# Revit family: Hager-Univers-IP55-D275-H2050-Cl.I-Steel_encl-NoHosted-PL-en
name_source: partatom
category: Equipement électrique
units: mm (PartAtom-declared; Revit-internal decimal feet)

## family parameters
Basée sur le plan de construction = Oui
Configuration du panneau = Deux colonnes, circuits au sein
Cote de connecteur circulaire = Utiliser le diamètre
Couper avec des vides une fois chargée = Non
Partagée = Non
Point de calcul de pièce = Non
Toujours verticalement = Oui
Type d'élément = Tableau de raccordement

## types (11) — shared parameters
Commentaires du type = Univers
EF000003 - Mounting method = EV012274 - Floor installation
EF000007 - Colour = EV000270 - Grey
EF000040 - Height = 2050 mm  [stored 6.72572 ft]
EF000049 - Depth = 275 mm
EF000116 - RAL-number = 7035
EF000118 - With mounting plate = Non
EF000266 - Number of rows = 12
EF000339 - Type of cover = EV004216 - Door
EF001088 - Extension possible = Oui
EF001131 - Internal depth = 275 mm
EF001596 - Material housing = EV000179 - Steel
EF001613 - Circuit integrity = EV000494 - None
EF002950 - Width in number of modular spacings = 24
EF003532 - Suitable for outdoor use = Non
EF004293 - Impact strength = EV008784 - IK10
EF005474 - Degree of protection (IP) = EV006420 - IP55
EF006306 - With lock = Non
EF007800 - Suitable for lightning protection = Non
EF008873 - Nominal current (In) = 800 A
EF009170 - Material plate thickness cabinet = 2 mm  [stored 0.00656168 ft]
EF009171 - Material plate thickness door/cover = 2 mm  [stored 0.00656168 ft]
EF009212 - Cover model = EV000116 - Closed
EF015940 - Cover with overpressure release = Non
Elévation par défaut = 1219 mm
Fabricant = Hager
HG000002 - With door or cover = Oui
HG000003 - Range = Univers
HG000006 - Flush mounted = Non
HG000023 - Double section enclosure = Non
HG000024 - Bottom section height = 600 mm
HG000026 - Floor standing = Oui
HG000027 - Plinth height = 200 mm  [stored 0.656168 ft]
zero-valued in all types: EF000218 - Built-in depth

## per-type parameters (varying)
| type | EF000008 - Width | EF000437 - Number of conduit inlets | EF004427 - Number of modules | EF004464 - Type of door | EF006244 - Transparent cover/door | EF009554 - Number of openings for flange plates | HG000004 - Manufacturer reference | HG000009 - Double swing door | HG000010 - Asymmetric doors |
| Floor installation IP55 W1050 H2050 D275  - FR24E2 | 1050 mm | 8 | 576 | EV003602 - Double | Non | 8 | FR24E2 | Oui | Oui |
| Floor installation IP55 W1050 H2050 D275  - FR24K2 | 1050 mm | 8 | 576 | EV003602 - Double | Oui | 8 | FR24K2 | Oui | Oui |
| Floor installation IP55 W1300 H2050 D275  - FR25E2 | 1300 mm  [stored 4.26509 ft] | 10 | 720 | EV003602 - Double | Non | 10 | FR25E2 | Oui | Oui |
| Floor installation IP55 W1300 H2050 D275  - FR25K2 | 1300 mm  [stored 4.26509 ft] | 10 | 720 | EV003602 - Double | Oui | 10 | FR25K2 | Oui | Oui |
| Floor installation IP55 W1550 H2050 D275  - FR26E2 | 1550 mm  [stored 5.0853 ft] | 12 | 864 | EV003602 - Double | Non | 12 | FR26E2 | Oui | Oui |
| Floor installation IP55 W1550 H2050 D275  - FR26K2 | 1550 mm  [stored 5.0853 ft] | 12 | 864 | EV003602 - Double | Oui | 12 | FR26K2 | Oui | Oui |
| Floor installation IP55 W300 H2050 D275  - FR21E2 | 300 mm | 2 | 144 | EV002646 - Single | Non | 2 | FR21E2 | Non | Non |
| Floor installation IP55 W550 H2050 D275  - FR22E2 | 550 mm | 4 | 288 | EV002646 - Single | Non | 4 | FR22E2 | Non | Non |
| Floor installation IP55 W550 H2050 D275  - FR22K2 | 550 mm | 4 | 288 | EV002646 - Single | Oui | 4 | FR22K2 | Non | Non |
| Floor installation IP55 W800 H2050 D275  - FR23E2 | 800 mm  [stored 2.62467 ft] | 6 | 432 | EV002646 - Single | Non | 6 | FR23E2 | Non | Non |
| Floor installation IP55 W800 H2050 D275  - FR23K2 | 800 mm  [stored 2.62467 ft] | 6 | 432 | EV002646 - Single | Oui | 6 | FR23K2 | Non | Non |

note: [stored X ft] marks values corroborated as IEEE doubles in the binary element streams (Revit-internal decimal feet)

## geometry (parser evidence)
native form markers: Blend x4, Sweep x11
no freeform markers — native parametric forms only
